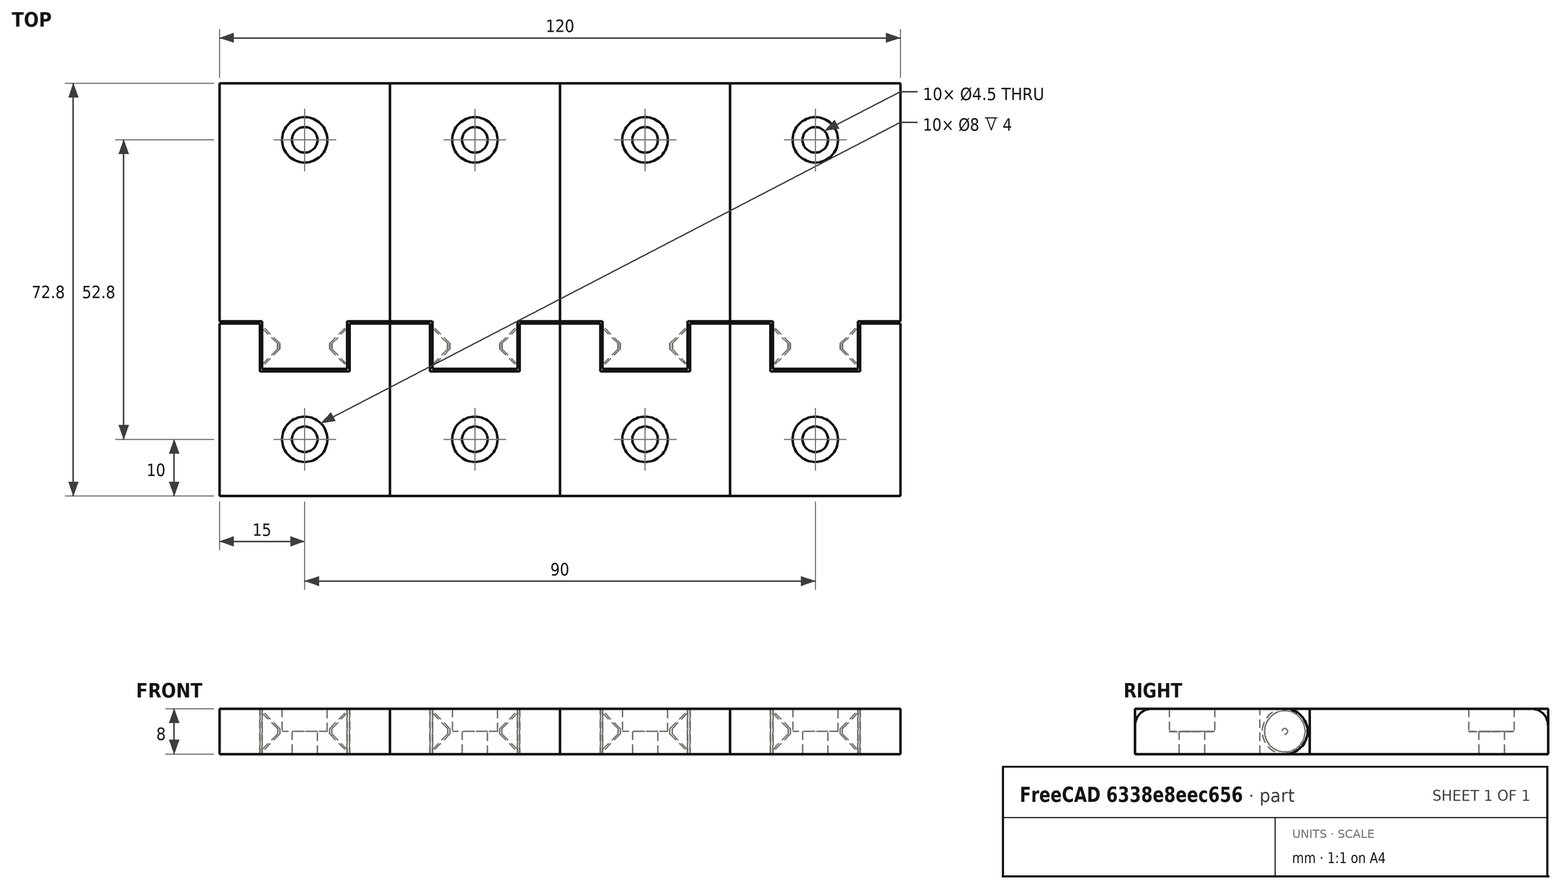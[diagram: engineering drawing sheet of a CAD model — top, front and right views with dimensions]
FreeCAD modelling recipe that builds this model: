
FCSTD DOCUMENT  (FreeCAD 1.0R1.0.1)
Label: Profile_Plexi_Hinge_001
License: All rights reserved
LicenseURL: http://en.wikipedia.org/wiki/All_rights_reserved
objects: Part::Cylinder×8, Part::MultiFuse×8, Part::Box×6, Part::Cut×6, Part::Cone×4, Part::Compound×3, Spreadsheet::Sheet×1, Part::FeaturePython×1
note: 35 computed .brp shape members not serialized (recipe doc carries the construction recipe); baked Part::Feature solids carry a one-line shape summary decoded from their .brp

FEATURE [Part::Box] Box  label="Cube"
  AttacherType = Attacher::AttachEngine3D
  Height = 8
  Length = 30
  Width = 26.4
  expr: Height = <<HingeParams>>.thickness
  expr: Length = <<HingeParams>>.h1 + <<HingeParams>>.h2
  expr: Width = <<HingeParams>>.e1 + <<HingeParams>>.thickness / 2 + <<HingeParams>>.gap
FEATURE [Part::Box] Box001  label="Cube001"
  AttacherType = Attacher::AttachEngine3D
  Height = 8
  Length = 15.8
  Placement = pos=(7.1,22,0) rot=(0,0,1;0rad)
  Width = 8.8
  expr: .Placement.Base.x = <<HingeParams>>.h2 / 2 - <<HingeParams>>.gap
  expr: .Placement.Base.y = <<HingeParams>>.e1
  expr: Height = <<HingeParams>>.thickness
  expr: Length = <<HingeParams>>.h1 + 2 * <<HingeParams>>.gap
  expr: Width = <<HingeParams>>.thickness + 2 * <<HingeParams>>.gap
FEATURE [Part::Box] Box002  label="Cube002"
  AttacherType = Attacher::AttachEngine3D
  Height = 8
  Length = 15
  Placement = pos=(7.5,26.4,0) rot=(0,0,1;0rad)
  Width = 46.2
  expr: .Placement.Base.x = <<HingeParams>>.h2 / 2
  expr: .Placement.Base.y = <<HingeParams>>.e1 + <<HingeParams>>.gap + <<HingeParams>>.thickness / 2
  expr: Height = <<HingeParams>>.thickness
  expr: Length = <<HingeParams>>.h1
  expr: Width = <<HingeParams>>.thickness / 2 + <<HingeParams>>.e2
FEATURE [Part::Box] Box003  label="Cube003"
  AttacherType = Attacher::AttachEngine3D
  Height = 8
  Length = 30
  Placement = pos=(0,30.8,0) rot=(0,0,1;0rad)
  Width = 42
  expr: .Placement.Base.y = <<HingeParams>>.e1 + <<HingeParams>>.thickness + <<HingeParams>>.gap * 2
  expr: Height = <<HingeParams>>.thickness
  expr: Length = <<HingeParams>>.h1 + <<HingeParams>>.h2
  expr: Width = <<HingeParams>>.e2 - <<HingeParams>>.gap / 2
FEATURE [Part::Cone] Cone
  Angle = 360
  AttacherType = Attacher::AttachEngine3D
  Height = 3.1
  Placement = pos=(10.2,26.4,4) rot=(0,1,0;-1.5708rad)
  Radius1 = 0.5
  Radius2 = 3.6
  expr: .Placement.Base.x = <<HingeParams>>.h2 / 2 - <<HingeParams>>.gap + <<HingeParams>>.thickness / 2 - <<HingeParams>>.gap - 0.5
  expr: .Placement.Base.y = <<HingeParams>>.e1 + <<HingeParams>>.gap + <<HingeParams>>.thickness / 2
  expr: .Placement.Base.z = <<HingeParams>>.thickness / 2
  expr: Height = <<HingeParams>>.thickness / 2 - <<HingeParams>>.gap - 0.5
  expr: Radius1 = 0.5
  expr: Radius2 = <<HingeParams>>.thickness / 2 - <<HingeParams>>.gap
FEATURE [Part::Cone] Cone002
  Angle = 360
  AttacherType = Attacher::AttachEngine3D
  Height = 3.5
  Placement = pos=(10.6,26.4,4) rot=(0,1,0;-1.5708rad)
  Radius1 = 0.5
  Radius2 = 4
  expr: .Placement.Base.x = <<HingeParams>>.h2 / 2 + <<HingeParams>>.thickness / 2 - <<HingeParams>>.gap - 0.5
  expr: .Placement.Base.y = <<HingeParams>>.e1 + <<HingeParams>>.gap + <<HingeParams>>.thickness / 2
  expr: .Placement.Base.z = <<HingeParams>>.thickness / 2
  expr: Height = <<HingeParams>>.thickness / 2 - 0.5
  expr: Radius1 = 0.5
  expr: Radius2 = <<HingeParams>>.thickness / 2
FEATURE [Part::Cone] Cone003
  Angle = 360
  AttacherType = Attacher::AttachEngine3D
  Height = 3.1
  Placement = pos=(19.8,26.4,4) rot=(0,1,0;1.5708rad)
  Radius1 = 0.5
  Radius2 = 3.6
  expr: .Placement.Base.x = <<HingeParams>>.h1 + <<HingeParams>>.h2 / 2 - (<<HingeParams>>.thickness / 2 - <<HingeParams>>.gap - 0.5) + <<HingeParams>>.gap
  expr: .Placement.Base.y = <<HingeParams>>.e1 + <<HingeParams>>.gap + <<HingeParams>>.thickness / 2
  expr: .Placement.Base.z = <<HingeParams>>.thickness / 2
  expr: Height = <<HingeParams>>.thickness / 2 - <<HingeParams>>.gap - 0.5
  expr: Radius1 = 0.5
  expr: Radius2 = <<HingeParams>>.thickness / 2 - <<HingeParams>>.gap
FEATURE [Part::Cone] Cone004
  Angle = 360
  AttacherType = Attacher::AttachEngine3D
  Height = 3.5
  Placement = pos=(19.4,26.4,4) rot=(0,1,0;1.5708rad)
  Radius1 = 0.5
  Radius2 = 4
  expr: .Placement.Base.x = <<HingeParams>>.h1 + <<HingeParams>>.h2 / 2 - (<<HingeParams>>.thickness / 2 - <<HingeParams>>.gap - 0.5)
  expr: .Placement.Base.y = <<HingeParams>>.e1 + <<HingeParams>>.gap + <<HingeParams>>.thickness / 2
  expr: .Placement.Base.z = <<HingeParams>>.thickness / 2
  expr: Height = <<HingeParams>>.thickness / 2 - 0.5
  expr: Radius1 = 0.5
  expr: Radius2 = <<HingeParams>>.thickness / 2
FEATURE [Part::Cylinder] Cylinder
  Angle = 360
  AttacherType = Attacher::AttachEngine3D
  FirstAngle = 0
  Height = 30
  Placement = pos=(0,26.4,4) rot=(0,1,0;1.5708rad)
  Radius = 4
  SecondAngle = 0
  expr: .Placement.Base.y = <<HingeParams>>.e1 + <<HingeParams>>.gap + <<HingeParams>>.thickness / 2
  expr: .Placement.Base.z = <<HingeParams>>.thickness / 2
  expr: Height = <<HingeParams>>.h1 + <<HingeParams>>.h2
  expr: Radius = <<HingeParams>>.thickness / 2
FEATURE [Part::Cylinder] Cylinder001
  Angle = 360
  AttacherType = Attacher::AttachEngine3D
  FirstAngle = 0
  Height = 15
  Placement = pos=(7.5,26.4,4) rot=(0,1,0;1.5708rad)
  Radius = 4
  SecondAngle = 0
  expr: .Placement.Base.x = <<HingeParams>>.h2 / 2
  expr: .Placement.Base.y = <<HingeParams>>.e1 + <<HingeParams>>.gap + <<HingeParams>>.thickness / 2
  expr: .Placement.Base.z = <<HingeParams>>.thickness / 2
  expr: Height = <<HingeParams>>.h1
  expr: Radius = <<HingeParams>>.thickness / 2
FEATURE [Part::MultiFuse] Fusion
  Shapes = -> [Box,Cylinder]
FEATURE [Part::Cut] Cut
  Base = -> Fusion
  Tool = -> Box001
FEATURE [Part::MultiFuse] Fusion001
  Shapes = -> [Cone,Cone003,Cut]
FEATURE [Part::MultiFuse] Fusion002
  Shapes = -> [Box003,Box002,Cylinder001]
FEATURE [Part::MultiFuse] Fusion003
  Shapes = -> [Cone004,Cone002]
FEATURE [Part::Cut] Cut001
  Base = -> Fusion002
  Tool = -> Fusion003
FEATURE [Part::Compound] Compound
  Links = -> [Fusion001,Cut001]
FEATURE [Spreadsheet::Sheet] Spreadsheet  label="HingeParams"
  cells = A2='Thickness; B2(thickness)=8; A3='Hinge length 1; B3(h1)=15; A4='Hinge length 2; B4(h2)=15; A5='Gap; B5(gap)=0.4; A6='Extend 1; B6(e1)=22; A7='Extend 2; B7(e2)=42.2
FEATURE [Part::Cylinder] Cylinder002
  Angle = 360
  AttacherType = Attacher::AttachEngine3D
  FirstAngle = 0
  Height = 10
  Placement = pos=(15,10,0) rot=(0,0,1;0rad)
  Radius = 2.25
  SecondAngle = 0
FEATURE [Part::Cylinder] Cylinder003
  Angle = 360
  AttacherType = Attacher::AttachEngine3D
  FirstAngle = 0
  Height = 4
  Placement = pos=(15,10,4) rot=(0,0,1;0rad)
  Radius = 4
  SecondAngle = 0
FEATURE [Part::MultiFuse] Fusion004
  Shapes = -> [Cylinder003,Cylinder002]
FEATURE [Part::Cylinder] Cylinder004
  Angle = 360
  AttacherType = Attacher::AttachEngine3D
  FirstAngle = 0
  Height = 10
  Placement = pos=(15,10,0) rot=(0,0,1;0rad)
  Radius = 2.25
  SecondAngle = 0
FEATURE [Part::Cylinder] Cylinder005
  Angle = 360
  AttacherType = Attacher::AttachEngine3D
  FirstAngle = 0
  Height = 4
  Placement = pos=(15,10,4) rot=(0,0,1;0rad)
  Radius = 4
  SecondAngle = 0
FEATURE [Part::MultiFuse] Fusion005
  Placement = pos=(0,52.8,0) rot=(0,0,1;0rad)
  Shapes = -> [Cylinder005,Cylinder004]
FEATURE [Part::MultiFuse] Fusion006
  Shapes = -> [Fusion004,Fusion005]
FEATURE [Part::Cut] Cut002
  Base = -> Compound
  Tool = -> Fusion006
FEATURE [Part::FeaturePython] Array  # Draft array (typed FeaturePython)
  AlwaysSyncPlacement = false
  Angle = 360
  ArrayType = 0
  Axis = (0,0,1)
  Base = -> Cut002
  Center = (0,0,0)
  Count = 4
  ExpandArray = false
  Fuse = false
  IntervalAxis = (0,0,0)
  IntervalX = (30,0,0)
  IntervalY = (0,100,0)
  IntervalZ = (0,0,100)
  NumberCircles = 3
  NumberPolar = 5
  NumberX = 4
  NumberY = 1
  NumberZ = 1
  PlacementList = 4 placements: arithmetic series from (0,0,0) step (30,0,0) to (90,0,0)
  RadialDistance = 50
  ScaleList = (4) [(1,1,1),(1,1,1),(1,1,1),(1,1,1)]
  Symmetry = 1
  TangentialDistance = 25
FEATURE [Part::Cylinder] Cylinder006
  Angle = 360
  AttacherType = Attacher::AttachEngine3D
  FirstAngle = 0
  Height = 120
  Radius = 3
  SecondAngle = 0
FEATURE [Part::Box] Box004  label="Cube004"
  AttacherType = Attacher::AttachEngine3D
  Height = 120
  Length = 10
  Width = 10
FEATURE [Part::Cut] Cut003
  Base = -> Box004
  Placement = pos=(0,0,0) rot=(0,1,0;1.5708rad)
  Tool = -> Cylinder006
FEATURE [Part::Compound] Compound001
  Links = -> [Cut003]
  Placement = pos=(0,3,5) rot=(1,0,0;3.14159rad)
FEATURE [Part::Box] Box005  label="Cube005"
  AttacherType = Attacher::AttachEngine3D
  Height = 120
  Length = 10
  Width = 10
FEATURE [Part::Cylinder] Cylinder007
  Angle = 360
  AttacherType = Attacher::AttachEngine3D
  FirstAngle = 0
  Height = 120
  Radius = 3
  SecondAngle = 0
FEATURE [Part::Cut] Cut004
  Base = -> Box005
  Placement = pos=(0,0,0) rot=(0,1,0;1.5708rad)
  Tool = -> Cylinder007
FEATURE [Part::Compound] Compound002
  Links = -> [Cut004]
  Placement = pos=(0,69.8,5) rot=(1,0,0;1.5708rad)
FEATURE [Part::MultiFuse] Fusion007
  Shapes = -> [Compound002,Compound001]
FEATURE [Part::Cut] Cut005
  Base = -> Array
  Tool = -> Fusion007
